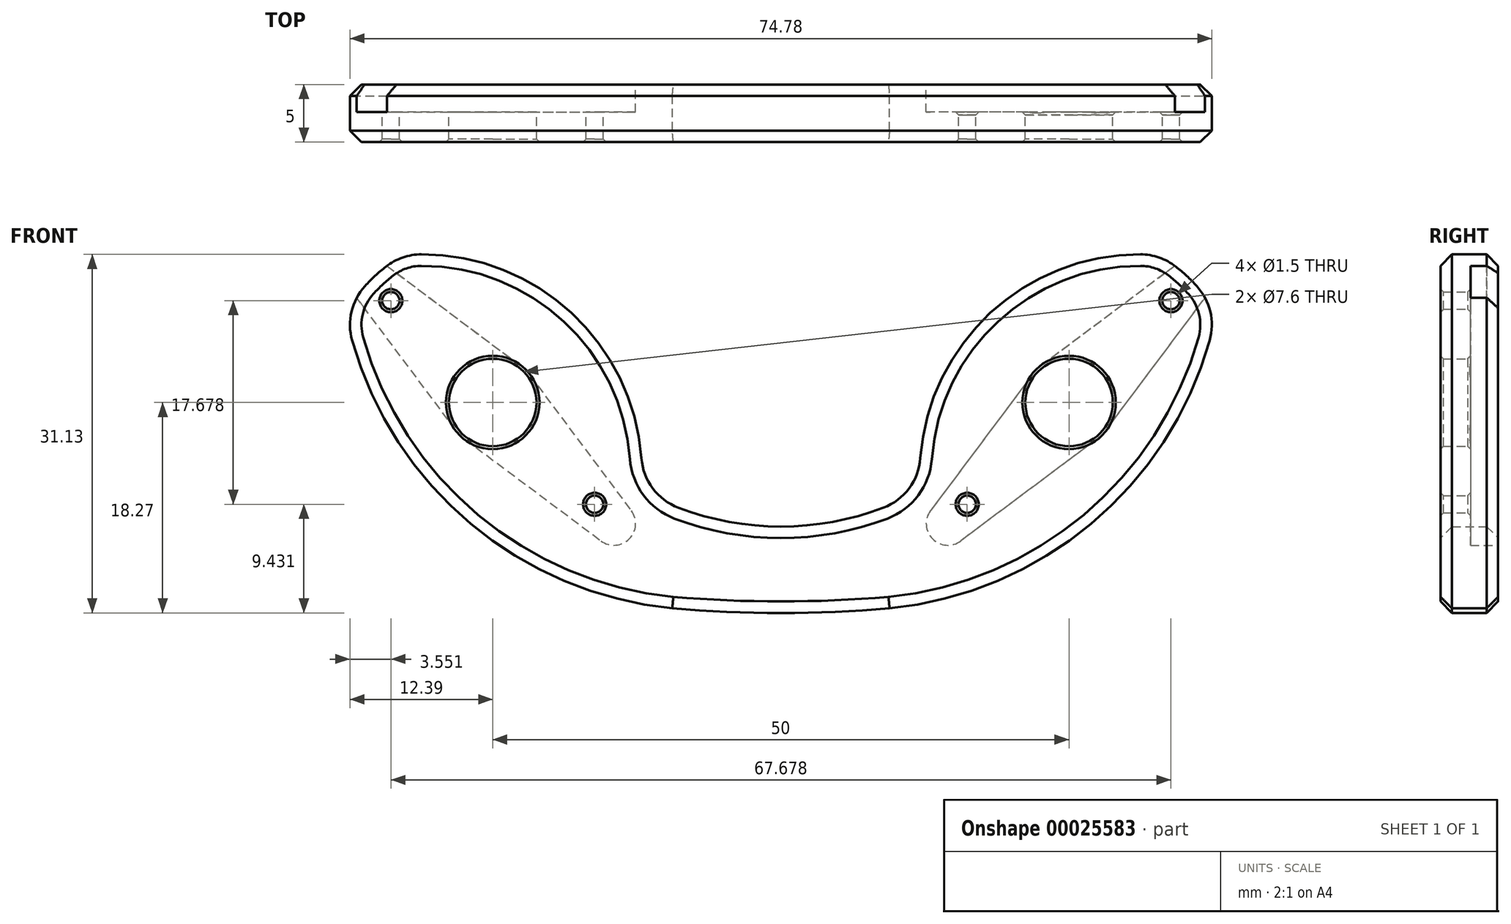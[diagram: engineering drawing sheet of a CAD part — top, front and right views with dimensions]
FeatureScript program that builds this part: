
annotation { "Feature Type Name" : "Feature", "Feature Type Description" : "" }
export const myFeature = defineFeature(function(context is Context, id is Id, definition is map)
    precondition{}
    {
        {
            var Q0;
            Q0=qCreatedBy(makeId("Front.planeOp"),FACE);
            var sketch = newSketch(context, id + "F0", { "sketchPlane" : qUnion([Q0])});
            skLineSegment(sketch, "E0", {"start": v(0, 0) * mm, "end": v(50, 0) * mm, "construction": true});
            skArc(sketch, "E1", {"start": v(62.79, 7.84) * mm, "mid": v(60.6, 10.6) * mm, "end": v(57.84, 12.79) * mm});
            skArc(sketch, "E2", {"start": v(15.58, -17.88) * mm, "mid": v(25, -18.27) * mm, "end": v(34.42, -17.88) * mm});
            skArc(sketch, "E3", {"start": v(12.9, -7.65) * mm, "mid": v(25, -10.77) * mm, "end": v(37.1, -7.65) * mm});
            skLineSegment(sketch, "E4", {"start": v(25, 14.23) * mm, "end": v(25, 93.85) * mm, "construction": true});
            skCircle(sketch, "E5", {"center": v(50, 0) * mm, "radius": 3.8 * mm});
            skLineSegment(sketch, "E6", {"start": v(50, 0) * mm, "end": v(58.84, 8.84) * mm, "construction": true});
            skLineSegment(sketch, "E7", {"start": v(50, 0) * mm, "end": v(41.16, -8.84) * mm, "construction": true});
            skCircle(sketch, "E8", {"center": v(58.84, 8.84) * mm, "radius": 0.75 * mm});
            skCircle(sketch, "E9", {"center": v(41.16, -8.84) * mm, "radius": 0.75 * mm});
            skArc(sketch, "E10", {"start": v(57.84, 12.79) * mm, "mid": v(42.74, 7.37) * mm, "end": v(37.1, -7.65) * mm});
            skArc(sketch, "E11", {"start": v(34.42, -17.88) * mm, "mid": v(52.85, -9.7) * mm, "end": v(62.79, 7.84) * mm});
            skCircle(sketch, "E12.MirrorC", {"center": v(-8.84, 8.84) * mm, "radius": 0.75 * mm});
            skCircle(sketch, "E13.MirrorC", {"center": v(8.84, -8.84) * mm, "radius": 0.75 * mm});
            skArc(sketch, "E14.MirrorCS", {"start": v(15.58, -17.88) * mm, "mid": v(-2.85, -9.7) * mm, "end": v(-12.79, 7.84) * mm});
            skLineSegment(sketch, "E15.MirrorCS", {"start": v(0, 0) * mm, "end": v(-8.84, 8.84) * mm});
            skArc(sketch, "E16.MirrorCS", {"start": v(-7.84, 12.79) * mm, "mid": v(7.26, 7.37) * mm, "end": v(12.9, -7.65) * mm});
            skLineSegment(sketch, "E17.MirrorCS", {"start": v(0, 0) * mm, "end": v(8.84, -8.84) * mm});
            skArc(sketch, "E18.MirrorCS", {"start": v(-12.79, 7.84) * mm, "mid": v(-10.6, 10.6) * mm, "end": v(-7.84, 12.79) * mm});
            skCircle(sketch, "E19.MirrorC", {"center": v(0, 0) * mm, "radius": 3.8 * mm});
            skSolve(sketch);
        }
        {
            var Q0;
            Q0=makeQuery(id+"F0.imprint","IMPRINT",FACE,{"disambiguationData":[TD([[makeQuery(id+"F0.imprint","IMPRINT",EDGE,{"derivedFrom":sQuery(id+"F0.wireOp",EDGE,"E1")}),1.0]])]});
            extrude(context, id + "F1", {"entities" : qUnion([Q0]), "depth" : 5 * mm});
        }
        {
            var Q0;
            Q0=makeQuery(id+"F1.opExtrude","SWEPT_EDGE",EDGE,{"disambiguationData":[OSD([sQuery(id+"F0.wireOp",EDGE,"3c59a44a-63db-4367-9b7c-f3897e68ae77"),sQuery(id+"F0.wireOp",EDGE,"E3")])]});
            var Q1;
            Q1=makeQuery(id+"F1.opExtrude","SWEPT_EDGE",EDGE,{"disambiguationData":[OSD([sQuery(id+"F0.wireOp",EDGE,"E1"),sQuery(id+"F0.wireOp",EDGE,"E3")])]});
            var Q2;
            Q2=makeQuery(id+"F1.opExtrude","SWEPT_EDGE",EDGE,{"disambiguationData":[OSD([sQuery(id+"F0.wireOp",EDGE,"E16.MirrorCS"),sQuery(id+"F0.wireOp",EDGE,"E18.MirrorCS")])]});
            var Q3;
            Q3=makeQuery(id+"F1.opExtrude","SWEPT_EDGE",EDGE,{"disambiguationData":[OSD([sQuery(id+"F0.wireOp",EDGE,"E14.MirrorCS"),sQuery(id+"F0.wireOp",EDGE,"E18.MirrorCS")])]});
            fillet(context, id + "F2", {"entities" : qUnion([Q0, Q1, Q2, Q3]), "radius" : 5 * mm, "tangentPropagation" : true, "allowEdgeOverflow" : false});
        }
        {
            var Q0;
            Q0=makeQuery(id+"F1.opExtrude","CAP_FACE",FACE,{"disambiguationData":[OSD([sQuery(id+"F0.wireOp",EDGE,"3c59a44a-63db-4367-9b7c-f3897e68ae77"),sQuery(id+"F0.wireOp",EDGE,"E1"),sQuery(id+"F0.wireOp",EDGE,"E2"),sQuery(id+"F0.wireOp",EDGE,"E3"),sQuery(id+"F0.wireOp",EDGE,"3b77c7ab-03fb-4d5e-bf77-a0c260f77105"),sQuery(id+"F0.wireOp",EDGE,"E5"),sQuery(id+"F0.wireOp",EDGE,"d05511cd-b470-4209-87b4-186450a734da"),sQuery(id+"F0.wireOp",EDGE,"9084bf2d-59ba-4467-81f1-71ae896b401c"),sQuery(id+"F0.wireOp",EDGE,"E8"),sQuery(id+"F0.wireOp",EDGE,"E9")])],"isStart":true});
            var sketch = newSketch(context, id + "F3", { "sketchPlane" : qUnion([Q0])});
            skLineSegment(sketch, "E20", {"start": v(0, 0) * mm, "end": v(10.52, 10.52) * mm, "construction": true});
            skLineSegment(sketch, "E21", {"start": v(0, 0) * mm, "end": v(-10.52, -10.52) * mm, "construction": true});
            skArc(sketch, "E22", {"start": v(-12.02, -9.4) * mm, "mid": v(-11.84, -11.84) * mm, "end": v(-9.4, -12.02) * mm});
            skArc(sketch, "E23", {"start": v(12.02, 9.4) * mm, "mid": v(11.84, 11.84) * mm, "end": v(9.4, 12.02) * mm});
            skArc(sketch, "E24", {"start": v(-2.4, 3.2) * mm, "mid": v(-2.83, 2.83) * mm, "end": v(-3.2, 2.4) * mm});
            skLineSegment(sketch, "E25", {"start": v(9.4, 12.02) * mm, "end": v(-2.4, 3.2) * mm});
            skLineSegment(sketch, "E26", {"start": v(3.2, -2.4) * mm, "end": v(12.02, 9.4) * mm});
            skLineSegment(sketch, "E27", {"start": v(-3.2, 2.4) * mm, "end": v(-12.02, -9.4) * mm});
            skLineSegment(sketch, "E28", {"start": v(2.4, -3.2) * mm, "end": v(-9.4, -12.02) * mm});
            skLineSegment(sketch, "E29", {"start": v(-50, 0) * mm, "end": v(0, 0) * mm, "construction": true});
            skLineSegment(sketch, "E30", {"start": v(-25, 0) * mm, "end": v(-25, 6.46) * mm, "construction": true});
            skArc(sketch, "E31.trimOffspring", {"start": v(2.4, -3.2) * mm, "mid": v(2.83, -2.83) * mm, "end": v(3.2, -2.4) * mm});
            skArc(sketch, "E32.MirrorCS", {"start": v(-47.6, 3.2) * mm, "mid": v(-47.17, 2.83) * mm, "end": v(-46.8, 2.4) * mm});
            skArc(sketch, "E33.MirrorCS", {"start": v(-52.4, -3.2) * mm, "mid": v(-52.83, -2.83) * mm, "end": v(-53.2, -2.4) * mm});
            skLineSegment(sketch, "E34.MirrorCS", {"start": v(-52.4, -3.2) * mm, "end": v(-40.6, -12.02) * mm});
            skLineSegment(sketch, "E35.MirrorCS", {"start": v(-50, 0) * mm, "end": v(-39.48, -10.52) * mm});
            skArc(sketch, "E36.MirrorCS", {"start": v(-62.02, 9.4) * mm, "mid": v(-61.84, 11.84) * mm, "end": v(-59.4, 12.02) * mm});
            skLineSegment(sketch, "E37.MirrorCS", {"start": v(-50, 0) * mm, "end": v(-60.52, 10.52) * mm});
            skLineSegment(sketch, "E38.MirrorCS", {"start": v(-53.2, -2.4) * mm, "end": v(-62.02, 9.4) * mm});
            skLineSegment(sketch, "E39.MirrorCS", {"start": v(-59.4, 12.02) * mm, "end": v(-47.6, 3.2) * mm});
            skArc(sketch, "E40.MirrorCS", {"start": v(-37.98, -9.4) * mm, "mid": v(-38.16, -11.84) * mm, "end": v(-40.6, -12.02) * mm});
            skLineSegment(sketch, "E41.MirrorCS", {"start": v(-46.8, 2.4) * mm, "end": v(-37.98, -9.4) * mm});
            skSolve(sketch);
        }
        {
            var Q0;
            Q0 = qSketchRegion(id + "F3", true);
            extrude(context, id + "F4", {"entities" : qUnion([Q0]), "operationType" : NewBodyOperationType.REMOVE, "oppositeDirection" : true, "depth" : 2.4 * mm});
        }
        {
            var Q0;
            Q0=makeQuery(id+"F4.boolean.opBoolean","INTERSECT",EDGE,{"derivedFrom":[makeQuery(id+"F1.opExtrude","SWEPT_FACE",FACE,{"disambiguationData":[OSD([sQuery(id+"F0.wireOp",EDGE,"E5")])]}),makeQuery(id+"F4.opExtrude","CAP_FACE",FACE,{"disambiguationData":[OSD([sQuery(id+"F3.wireOp",EDGE,"E32.MirrorCS"),sQuery(id+"F3.wireOp",EDGE,"E33.MirrorCS"),sQuery(id+"F3.wireOp",EDGE,"E34.MirrorCS"),sQuery(id+"F3.wireOp",EDGE,"E36.MirrorCS"),sQuery(id+"F3.wireOp",EDGE,"E38.MirrorCS"),sQuery(id+"F3.wireOp",EDGE,"E39.MirrorCS"),sQuery(id+"F3.wireOp",EDGE,"E40.MirrorCS"),sQuery(id+"F3.wireOp",EDGE,"E41.MirrorCS")])],"isStart":false})]});
            var Q1;
            Q1=makeQuery(id+"F1.opExtrude","CAP_EDGE",EDGE,{"disambiguationData":[OSD([sQuery(id+"F0.wireOp",EDGE,"E5")])],"isStart":false});
            var Q2;
            Q2=makeQuery(id+"F4.boolean.opBoolean","INTERSECT",EDGE,{"derivedFrom":[makeQuery(id+"F1.opExtrude","SWEPT_FACE",FACE,{"disambiguationData":[OSD([sQuery(id+"F0.wireOp",EDGE,"3b77c7ab-03fb-4d5e-bf77-a0c260f77105")])]}),makeQuery(id+"F4.opExtrude","CAP_FACE",FACE,{"disambiguationData":[OSD([sQuery(id+"F3.wireOp",EDGE,"E22"),sQuery(id+"F3.wireOp",EDGE,"E23"),sQuery(id+"F3.wireOp",EDGE,"E24"),sQuery(id+"F3.wireOp",EDGE,"E25"),sQuery(id+"F3.wireOp",EDGE,"E26"),sQuery(id+"F3.wireOp",EDGE,"E27"),sQuery(id+"F3.wireOp",EDGE,"E28"),sQuery(id+"F3.wireOp",EDGE,"E31.trimOffspring")])],"isStart":false})]});
            var Q3;
            Q3=makeQuery(id+"F1.opExtrude","CAP_EDGE",EDGE,{"disambiguationData":[OSD([sQuery(id+"F0.wireOp",EDGE,"3b77c7ab-03fb-4d5e-bf77-a0c260f77105")])],"isStart":false});
            var Q4;
            Q4=makeQuery(id+"F4.boolean.opBoolean","COPY",EDGE,{"derivedFrom":makeQuery(id+"F4.opExtrude","CAP_EDGE",EDGE,{"disambiguationData":[OSD([sQuery(id+"F3.wireOp",EDGE,"E39.MirrorCS")])],"isStart":true})});
            var Q5;
            Q5=makeQuery(id+"F4.boolean.opBoolean","COPY",EDGE,{"derivedFrom":makeQuery(id+"F4.opExtrude","CAP_EDGE",EDGE,{"disambiguationData":[OSD([sQuery(id+"F3.wireOp",EDGE,"E26")])],"isStart":true})});
            var Q6;
            Q6=makeQuery(id+"F1.opExtrude","CAP_EDGE",EDGE,{"disambiguationData":[OSD([sQuery(id+"F0.wireOp",EDGE,"d05511cd-b470-4209-87b4-186450a734da")])],"isStart":false});
            var Q7;
            Q7=makeQuery(id+"F1.opExtrude","CAP_EDGE",EDGE,{"disambiguationData":[OSD([sQuery(id+"F0.wireOp",EDGE,"9084bf2d-59ba-4467-81f1-71ae896b401c")])],"isStart":false});
            var Q8;
            Q8=makeQuery(id+"F1.opExtrude","CAP_EDGE",EDGE,{"disambiguationData":[OSD([sQuery(id+"F0.wireOp",EDGE,"E8")])],"isStart":false});
            var Q9;
            Q9=makeQuery(id+"F1.opExtrude","CAP_EDGE",EDGE,{"disambiguationData":[OSD([sQuery(id+"F0.wireOp",EDGE,"E9")])],"isStart":false});
            var Q10;
            Q10=makeQuery(id+"F1.opExtrude","CAP_EDGE",EDGE,{"disambiguationData":[OSD([sQuery(id+"F0.wireOp",EDGE,"E13.MirrorC")])],"isStart":false});
            var Q11;
            Q11=makeQuery(id+"F1.opExtrude","CAP_EDGE",EDGE,{"disambiguationData":[OSD([sQuery(id+"F0.wireOp",EDGE,"E12.MirrorC")])],"isStart":false});
            var Q12;
            Q12=makeQuery(id+"F1.opExtrude","CAP_EDGE",EDGE,{"disambiguationData":[OSD([sQuery(id+"F0.wireOp",EDGE,"E19.MirrorC")])],"isStart":false});
            var Q13;
            Q13=makeQuery(id+"F4.boolean.opBoolean","INTERSECT",EDGE,{"derivedFrom":[makeQuery(id+"F1.opExtrude","SWEPT_FACE",FACE,{"disambiguationData":[OSD([sQuery(id+"F0.wireOp",EDGE,"E9")])]}),makeQuery(id+"F4.opExtrude","CAP_FACE",FACE,{"disambiguationData":[OSD([sQuery(id+"F3.wireOp",EDGE,"E32.MirrorCS"),sQuery(id+"F3.wireOp",EDGE,"E33.MirrorCS"),sQuery(id+"F3.wireOp",EDGE,"E34.MirrorCS"),sQuery(id+"F3.wireOp",EDGE,"E36.MirrorCS"),sQuery(id+"F3.wireOp",EDGE,"E38.MirrorCS"),sQuery(id+"F3.wireOp",EDGE,"E39.MirrorCS"),sQuery(id+"F3.wireOp",EDGE,"E40.MirrorCS"),sQuery(id+"F3.wireOp",EDGE,"E41.MirrorCS")])],"isStart":false})]});
            var Q14;
            Q14=makeQuery(id+"F4.boolean.opBoolean","INTERSECT",EDGE,{"derivedFrom":[makeQuery(id+"F1.opExtrude","SWEPT_FACE",FACE,{"disambiguationData":[OSD([sQuery(id+"F0.wireOp",EDGE,"E8")])]}),makeQuery(id+"F4.opExtrude","CAP_FACE",FACE,{"disambiguationData":[OSD([sQuery(id+"F3.wireOp",EDGE,"E32.MirrorCS"),sQuery(id+"F3.wireOp",EDGE,"E33.MirrorCS"),sQuery(id+"F3.wireOp",EDGE,"E34.MirrorCS"),sQuery(id+"F3.wireOp",EDGE,"E36.MirrorCS"),sQuery(id+"F3.wireOp",EDGE,"E38.MirrorCS"),sQuery(id+"F3.wireOp",EDGE,"E39.MirrorCS"),sQuery(id+"F3.wireOp",EDGE,"E40.MirrorCS"),sQuery(id+"F3.wireOp",EDGE,"E41.MirrorCS")])],"isStart":false})]});
            chamfer(context, id + "F5", {"entities" : qUnion([Q0, Q1, Q2, Q3, Q4, Q5, Q6, Q7, Q8, Q9, Q10, Q11, Q12, Q13, Q14]), "width" : 0.25 * mm, "tangentPropagation" : true});
        }
        {
            var Q0;
            Q0=makeQuery(id+"F1.opExtrude","CAP_EDGE",EDGE,{"disambiguationData":[OSD([sQuery(id+"F0.wireOp",EDGE,"E14.MirrorCS")])],"isStart":false});
            var Q1;
            Q1=makeQuery(id+"F1.opExtrude","CAP_EDGE",EDGE,{"disambiguationData":[OSD([sQuery(id+"F0.wireOp",EDGE,"E2")])],"isStart":false});
            var Q2;
            Q2=makeQuery(id+"F1.opExtrude","CAP_EDGE",EDGE,{"disambiguationData":[OSD([sQuery(id+"F0.wireOp",EDGE,"E14.MirrorCS")])],"isStart":true});
            var Q3;
            Q3=makeQuery(id+"F1.opExtrude","CAP_EDGE",EDGE,{"disambiguationData":[OSD([sQuery(id+"F0.wireOp",EDGE,"E11")])],"isStart":true});
            var Q4;
            Q4=makeQuery(id+"F1.opExtrude","CAP_EDGE",EDGE,{"disambiguationData":[OSD([sQuery(id+"F0.wireOp",EDGE,"E10")])],"isStart":true});
            chamfer(context, id + "F6", {"entities" : qUnion([Q0, Q1, Q2, Q3, Q4]), "width" : 1 * mm, "tangentPropagation" : true});
        }
    });
